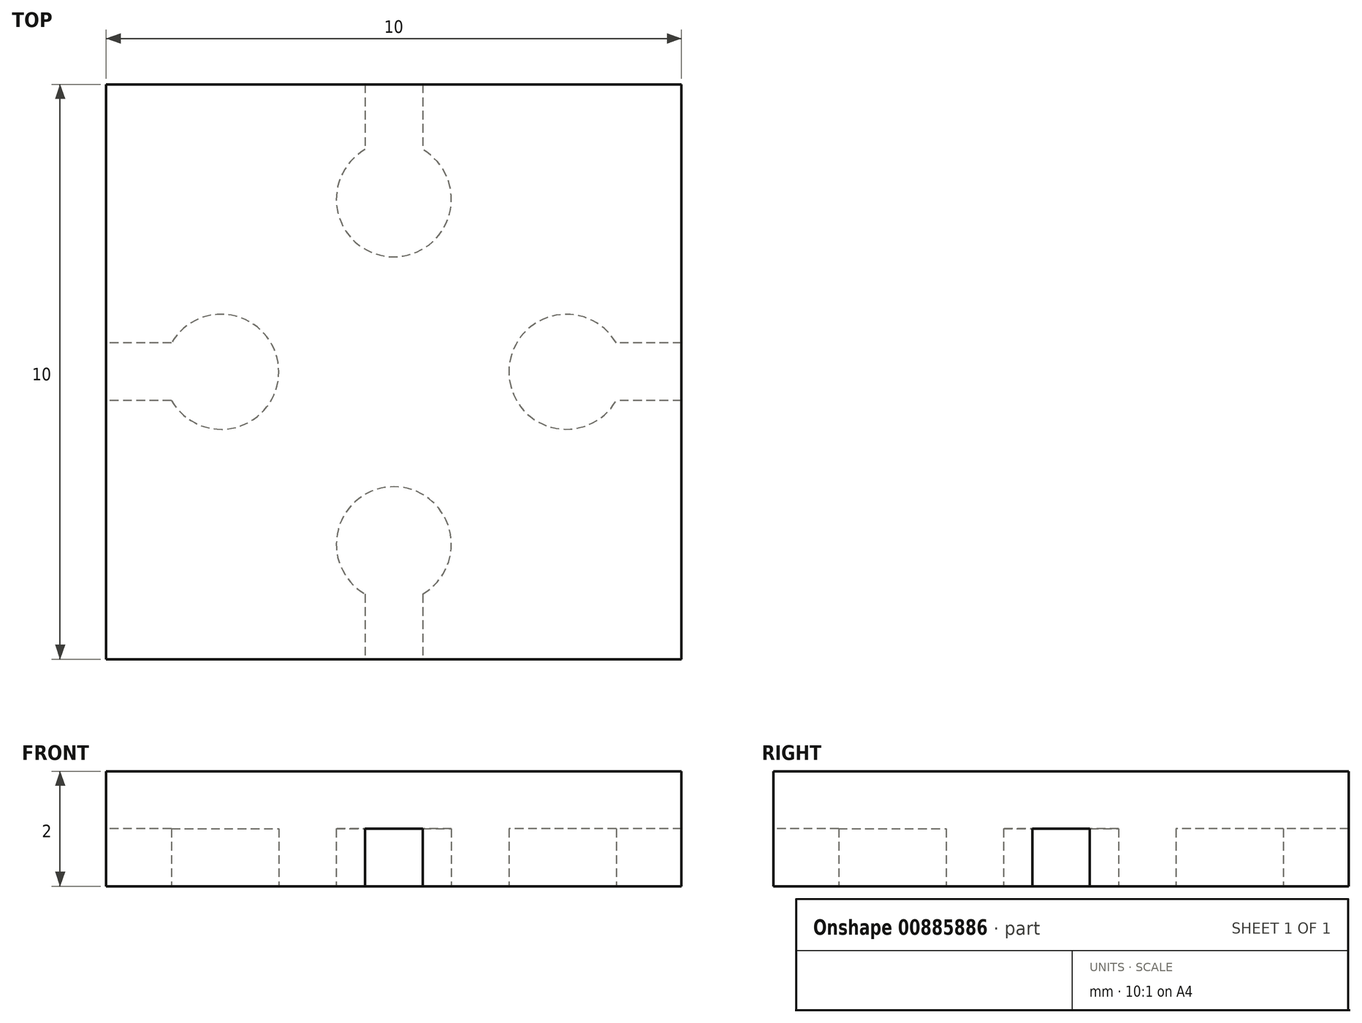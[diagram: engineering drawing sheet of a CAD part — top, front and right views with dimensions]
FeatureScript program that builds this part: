
annotation { "Feature Type Name" : "Feature", "Feature Type Description" : "" }
export const myFeature = defineFeature(function(context is Context, id is Id, definition is map)
    precondition{}
    {
        {
            var Q0;
            Q0=qCreatedBy(makeId("Top.planeOp"),FACE);
            var sketch = newSketch(context, id + "F0", { "sketchPlane" : qUnion([Q0])});
            skLineSegment(sketch, "E0.bottom", {"start": v(5, -5) * mm, "end": v(-5, -5) * mm});
            skLineSegment(sketch, "E0.top", {"start": v(5, 5) * mm, "end": v(-5, 5) * mm});
            skLineSegment(sketch, "E0.left", {"start": v(5, -5) * mm, "end": v(5, 5) * mm});
            skLineSegment(sketch, "E0.right", {"start": v(-5, -5) * mm, "end": v(-5, 5) * mm});
            skPoint(sketch, "E0.middle", {"position": v(0, 0) * mm});
            skSolve(sketch);
        }
        {
            var Q0;
            Q0 = qSketchRegion(id + "F0", true);
            extrude(context, id + "F1", {"entities" : qUnion([Q0]), "depth" : 2 * mm, "offsetDistance" : 25 * mm});
        }
        {
            var Q0;
            Q0=makeQuery(id+"F1.opExtrude","CAP_FACE",FACE,{"disambiguationData":[OSD([sQuery(id+"F0.wireOp",EDGE,"E0.bottom"),sQuery(id+"F0.wireOp",EDGE,"E0.top"),sQuery(id+"F0.wireOp",EDGE,"E0.left"),sQuery(id+"F0.wireOp",EDGE,"E0.right")])],"isStart":true});
            var sketch = newSketch(context, id + "F2", { "sketchPlane" : qUnion([Q0])});
            skCircle(sketch, "E1", {"center": v(0, 3) * mm, "radius": 1 * mm});
            skCircle(sketch, "E2", {"center": v(3, 0) * mm, "radius": 1 * mm});
            skCircle(sketch, "E3", {"center": v(0, -3) * mm, "radius": 1 * mm});
            skCircle(sketch, "E4", {"center": v(-3, 0) * mm, "radius": 1 * mm});
            skLineSegment(sketch, "E5.bottom", {"start": v(5, -0.5) * mm, "end": v(3, -0.5) * mm});
            skLineSegment(sketch, "E5.top", {"start": v(5, 0.5) * mm, "end": v(3, 0.5) * mm});
            skLineSegment(sketch, "E5.left", {"start": v(5, -0.5) * mm, "end": v(5, 0.5) * mm});
            skLineSegment(sketch, "E5.right", {"start": v(3, -0.5) * mm, "end": v(3, 0.5) * mm});
            skPoint(sketch, "E5.middle", {"position": v(4, 0) * mm});
            skLineSegment(sketch, "E6.bottom", {"start": v(0.5, 3) * mm, "end": v(-0.5, 3) * mm});
            skLineSegment(sketch, "E6.top", {"start": v(0.5, 5) * mm, "end": v(-0.5, 5) * mm});
            skLineSegment(sketch, "E6.left", {"start": v(0.5, 3) * mm, "end": v(0.5, 5) * mm});
            skLineSegment(sketch, "E6.right", {"start": v(-0.5, 3) * mm, "end": v(-0.5, 5) * mm});
            skPoint(sketch, "E6.middle", {"position": v(0, 4) * mm});
            skLineSegment(sketch, "E7.bottom", {"start": v(-3, -0.5) * mm, "end": v(-5, -0.5) * mm});
            skLineSegment(sketch, "E7.top", {"start": v(-3, 0.5) * mm, "end": v(-5, 0.5) * mm});
            skLineSegment(sketch, "E7.left", {"start": v(-3, -0.5) * mm, "end": v(-3, 0.5) * mm});
            skLineSegment(sketch, "E7.right", {"start": v(-5, -0.5) * mm, "end": v(-5, 0.5) * mm});
            skPoint(sketch, "E7.middle", {"position": v(-4, 0) * mm});
            skLineSegment(sketch, "E8.bottom", {"start": v(0.5, -5) * mm, "end": v(-0.5, -5) * mm});
            skLineSegment(sketch, "E8.top", {"start": v(0.5, -3) * mm, "end": v(-0.5, -3) * mm});
            skLineSegment(sketch, "E8.left", {"start": v(0.5, -5) * mm, "end": v(0.5, -3) * mm});
            skLineSegment(sketch, "E8.right", {"start": v(-0.5, -5) * mm, "end": v(-0.5, -3) * mm});
            skPoint(sketch, "E8.middle", {"position": v(0, -4) * mm});
            skSolve(sketch);
        }
        {
            var Q0;
            Q0 = qSketchRegion(id + "F2", true);
            extrude(context, id + "F3", {"entities" : qUnion([Q0]), "operationType" : NewBodyOperationType.REMOVE, "oppositeDirection" : true, "depth" : 1 * mm, "offsetDistance" : 25 * mm});
        }
    });
